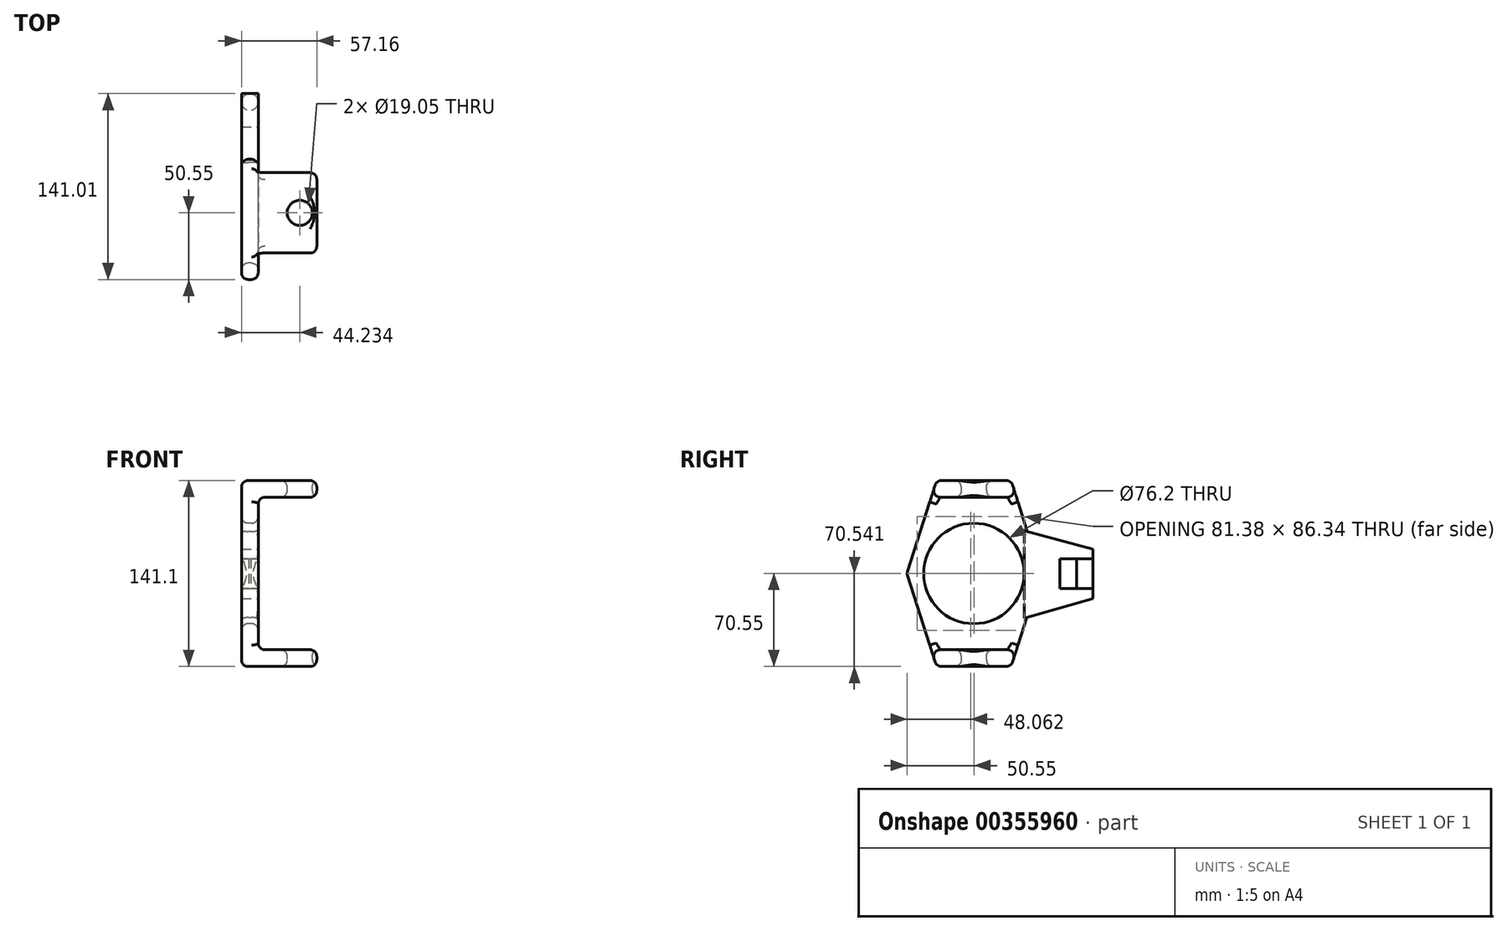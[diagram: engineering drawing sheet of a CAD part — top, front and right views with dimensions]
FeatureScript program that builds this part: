
annotation { "Feature Type Name" : "Feature", "Feature Type Description" : "" }
export const myFeature = defineFeature(function(context is Context, id is Id, definition is map)
    precondition{}
    {
        {
            var Q0;
            Q0=qCreatedBy(makeId("Front.planeOp"),FACE);
            var sketch = newSketch(context, id + "F0", { "sketchPlane" : qUnion([Q0])});
            skLineSegment(sketch, "E0.bottom", {"start": v(22.22, 57.85) * mm, "end": v(-22.23, 57.85) * mm});
            skLineSegment(sketch, "E0.top", {"start": v(22.22, -57.85) * mm, "end": v(-22.23, -57.85) * mm});
            skLineSegment(sketch, "E0.right", {"start": v(-22.23, 57.85) * mm, "end": v(-22.23, -57.85) * mm});
            skPoint(sketch, "E0.middle", {"position": v(0, 0) * mm});
            skLineSegment(sketch, "E1.0", {"start": v(22.22, -70.55) * mm, "end": v(-34.93, -70.55) * mm});
            skLineSegment(sketch, "E1.1", {"start": v(-34.93, 70.55) * mm, "end": v(-34.93, -70.55) * mm});
            skLineSegment(sketch, "E1.2", {"start": v(22.22, 70.55) * mm, "end": v(-34.93, 70.55) * mm});
            skLineSegment(sketch, "E2", {"start": v(22.22, 70.55) * mm, "end": v(22.22, 57.85) * mm});
            skLineSegment(sketch, "E3", {"start": v(22.22, -57.85) * mm, "end": v(22.22, -70.55) * mm});
            skSolve(sketch);
        }
        {
            var Q0;
            Q0=makeQuery(id+"F0.imprint","IMPRINT",FACE,{"disambiguationData":[TD([[makeQuery(id+"F0.imprint","IMPRINT",EDGE,{"derivedFrom":sQuery(id+"F0.wireOp",EDGE,"E0.bottom")}),-1.0]])]});
            extrude(context, id + "F1", {"entities" : qUnion([Q0]), "depth" : 101.6 * mm});
        }
        {
            var Q0;
            Q0=makeQuery(id+"F1.opExtrude","SWEPT_FACE",FACE,{"disambiguationData":[OSD([sQuery(id+"F0.wireOp",EDGE,"E1.1")])]});
            var sketch = newSketch(context, id + "F2", { "sketchPlane" : qUnion([Q0])});
            skCircle(sketch, "E4", {"center": v(50.8, 0) * mm, "radius": 38.1 * mm});
            skPoint(sketch, "E4.centerSnap0", {"position": v(50.8, -70.55) * mm});
            skLineSegment(sketch, "E5.bottom", {"start": v(79.08, -70.55) * mm, "end": v(22.52, -70.55) * mm, "construction": true});
            skLineSegment(sketch, "E5.top", {"start": v(79.08, 70.55) * mm, "end": v(22.52, 70.55) * mm, "construction": true});
            skLineSegment(sketch, "E5.left", {"start": v(79.08, -70.55) * mm, "end": v(79.08, 70.55) * mm, "construction": true});
            skLineSegment(sketch, "E5.right", {"start": v(22.52, -70.55) * mm, "end": v(22.52, 70.55) * mm, "construction": true});
            skLineSegment(sketch, "E6", {"start": v(79.08, -70.55) * mm, "end": v(101.6, 0) * mm});
            skLineSegment(sketch, "E7", {"start": v(101.6, 0) * mm, "end": v(79.08, 70.55) * mm});
            skLineSegment(sketch, "E8", {"start": v(22.52, 70.55) * mm, "end": v(0, 0) * mm});
            skLineSegment(sketch, "E9", {"start": v(0, 0) * mm, "end": v(22.52, -70.55) * mm});
            skSolve(sketch);
        }
        {
            var Q0;
            {var subQ0=sQuery(id+"F2.wireOp",EDGE,"E9");Q0=makeQuery(id+"F2.imprint","IMPRINT",FACE,{"disambiguationData":[TD([[makeQuery(id+"F2.imprint","IMPRINT",EDGE,{"derivedFrom":subQ0}),-1.0]])]});}
            var Q1;
            {var subQ0=sQuery(id+"F2.wireOp",EDGE,"E8");Q1=makeQuery(id+"F2.imprint","IMPRINT",FACE,{"disambiguationData":[TD([[makeQuery(id+"F2.imprint","IMPRINT",EDGE,{"derivedFrom":subQ0}),-1.0]])]});}
            var Q2;
            {var subQ0=sQuery(id+"F2.wireOp",EDGE,"E7");Q2=makeQuery(id+"F2.imprint","IMPRINT",FACE,{"disambiguationData":[TD([[makeQuery(id+"F2.imprint","IMPRINT",EDGE,{"derivedFrom":subQ0}),-1.0]])]});}
            var Q3;
            {var subQ0=sQuery(id+"F2.wireOp",EDGE,"E6");Q3=makeQuery(id+"F2.imprint","IMPRINT",FACE,{"disambiguationData":[TD([[makeQuery(id+"F2.imprint","IMPRINT",EDGE,{"derivedFrom":subQ0}),-1.0]])]});}
            var Q4;
            Q4=makeQuery(id+"F2.imprint","IMPRINT",FACE,{"disambiguationData":[TD([[makeQuery(id+"F2.imprint","IMPRINT",EDGE,{"derivedFrom":sQuery(id+"F2.wireOp",EDGE,"E4")}),1.0]])]});
            extrude(context, id + "F3", {"entities" : qUnion([Q0, Q1, Q2, Q3, Q4]), "operationType" : NewBodyOperationType.REMOVE, "endBound" : BoundingType.THROUGH_ALL, "oppositeDirection" : true, "depth" : 25.4 * mm});
        }
        {
            var Q0;
            Q0=makeQuery(id+"F1.opExtrude","SWEPT_FACE",FACE,{"disambiguationData":[OSD([sQuery(id+"F0.wireOp",EDGE,"E1.2")])]});
            var sketch = newSketch(context, id + "F4", { "sketchPlane" : qUnion([Q0])});
            skCircle(sketch, "E10", {"center": v(9.3, -50.8) * mm, "radius": 9.53 * mm});
            skPoint(sketch, "E10.centerSnap0", {"position": v(22.22, -50.8) * mm});
            skSolve(sketch);
        }
        {
            var Q0;
            Q0=makeQuery(id+"F4.imprint","IMPRINT",FACE,{"disambiguationData":[TD([[makeQuery(id+"F4.imprint","IMPRINT",EDGE,{"derivedFrom":sQuery(id+"F4.wireOp",EDGE,"E10")}),1.0]])]});
            extrude(context, id + "F5", {"entities" : qUnion([Q0]), "operationType" : NewBodyOperationType.REMOVE, "endBound" : BoundingType.THROUGH_ALL, "oppositeDirection" : true, "depth" : 25.4 * mm});
        }
        {
            var Q0;
            Q0=makeQuery(id+"F3.boolean.opBoolean","COPY",EDGE,{"derivedFrom":makeQuery(id+"F3.opExtrude","SWEPT_EDGE",EDGE,{"disambiguationData":[OSD([sQuery(id+"F0.wireOp",EDGE,"E1.1"),sQuery(id+"F0.wireOp",EDGE,"E1.2"),sQuery(id+"F2.wireOp",EDGE,"E8")])]})});
            var Q1;
            Q1=makeQuery(id+"F1.opExtrude","SWEPT_EDGE",EDGE,{"disambiguationData":[OSD([sQuery(id+"F0.wireOp",EDGE,"E1.1"),sQuery(id+"F0.wireOp",EDGE,"E1.2")])]});
            var Q2;
            Q2=makeQuery(id+"F3.boolean.opBoolean","COPY",EDGE,{"derivedFrom":makeQuery(id+"F3.opExtrude","SWEPT_EDGE",EDGE,{"disambiguationData":[OSD([sQuery(id+"F0.wireOp",EDGE,"E1.1"),sQuery(id+"F0.wireOp",EDGE,"E1.2"),sQuery(id+"F2.wireOp",EDGE,"E7")])]})});
            var Q3;
            Q3=makeQuery(id+"F1.opExtrude","SWEPT_EDGE",EDGE,{"disambiguationData":[OSD([sQuery(id+"F0.wireOp",EDGE,"E1.2"),sQuery(id+"F0.wireOp",EDGE,"E2")])]});
            var Q4;
            Q4=makeQuery(id+"F1.opExtrude","SWEPT_FACE",FACE,{"disambiguationData":[OSD([sQuery(id+"F0.wireOp",EDGE,"E1.1")])]});
            var Q5;
            Q5=makeQuery(id+"F3.boolean.opBoolean","COPY",FACE,{"derivedFrom":makeQuery(id+"F3.opExtrude","SWEPT_FACE",FACE,{"disambiguationData":[OSD([sQuery(id+"F2.wireOp",EDGE,"E8")])]})});
            var Q6;
            Q6=makeQuery(id+"F3.boolean.opBoolean","COPY",FACE,{"derivedFrom":makeQuery(id+"F3.opExtrude","SWEPT_FACE",FACE,{"disambiguationData":[OSD([sQuery(id+"F2.wireOp",EDGE,"E9")])]})});
            var Q7;
            Q7=makeQuery(id+"F1.opExtrude","SWEPT_FACE",FACE,{"disambiguationData":[OSD([sQuery(id+"F0.wireOp",EDGE,"E1.0")])]});
            var Q8;
            Q8=makeQuery(id+"F3.boolean.opBoolean","COPY",FACE,{"derivedFrom":makeQuery(id+"F3.opExtrude","SWEPT_FACE",FACE,{"disambiguationData":[OSD([sQuery(id+"F2.wireOp",EDGE,"E6")])]})});
            var Q9;
            Q9=makeQuery(id+"F3.boolean.opBoolean","COPY",FACE,{"derivedFrom":makeQuery(id+"F3.opExtrude","SWEPT_FACE",FACE,{"disambiguationData":[OSD([sQuery(id+"F2.wireOp",EDGE,"E7")])]})});
            var Q10;
            Q10=makeQuery(id+"F1.opExtrude","SWEPT_FACE",FACE,{"disambiguationData":[OSD([sQuery(id+"F0.wireOp",EDGE,"E0.bottom")])]});
            var Q11;
            Q11=makeQuery(id+"F1.opExtrude","SWEPT_FACE",FACE,{"disambiguationData":[OSD([sQuery(id+"F0.wireOp",EDGE,"E0.top")])]});
            var Q12;
            Q12=makeQuery(id+"F1.opExtrude","SWEPT_FACE",FACE,{"disambiguationData":[OSD([sQuery(id+"F0.wireOp",EDGE,"E1.2")])]});
            var Q13;
            Q13=makeQuery(id+"F3.boolean.opBoolean","INTERSECT",EDGE,{"derivedFrom":[makeQuery(id+"F1.opExtrude","SWEPT_FACE",FACE,{"disambiguationData":[OSD([sQuery(id+"F0.wireOp",EDGE,"E0.right")])]}),makeQuery(id+"F3.opExtrude","SWEPT_FACE",FACE,{"disambiguationData":[OSD([sQuery(id+"F2.wireOp",EDGE,"E4")])]})]});
            fillet(context, id + "F6", {"entities" : qUnion([Q0, Q1, Q2, Q3, Q4, Q5, Q6, Q7, Q8, Q9, Q10, Q11, Q12, Q13]), "radius" : 5.08 * mm, "tangentPropagation" : true, "allowEdgeOverflow" : false});
        }
        {
            var Q0;
            Q0=qCreatedBy(makeId("Right.planeOp"),FACE);
            var sketch = newSketch(context, id + "F7", { "sketchPlane" : qUnion([Q0])});
            skLineSegment(sketch, "E11.left", {"start": v(-12.6, 32.52) * mm, "end": v(-12.6, -33.96) * mm});
            skLineSegment(sketch, "E12.right", {"start": v(-12.6, -11.3) * mm, "end": v(-12.6, 11.3) * mm, "construction": true});
            skPoint(sketch, "E12.middle", {"position": v(27.22, 0) * mm});
            skPoint(sketch, "E12.middle.positionSnap0", {"position": v(27.22, 32.52) * mm});
            skPoint(sketch, "E12.centerSnap0", {"position": v(27.22, 32.52) * mm});
            skLineSegment(sketch, "E13", {"start": v(-12.6, 32.52) * mm, "end": v(39.66, 18.6) * mm});
            skLineSegment(sketch, "E14", {"start": v(39.66, -19.09) * mm, "end": v(-12.6, -33.96) * mm});
            skLineSegment(sketch, "E15", {"start": v(39.66, 18.6) * mm, "end": v(39.66, 11.3) * mm});
            skLineSegment(sketch, "E16.trimOffspring", {"start": v(39.66, -11.3) * mm, "end": v(39.66, -19.09) * mm});
            skLineSegment(sketch, "E17", {"start": v(39.66, -19.09) * mm, "end": v(39.66, -11.3) * mm});
            skLineSegment(sketch, "E18.bottom", {"start": v(39.66, -11.3) * mm, "end": v(14.3, -11.3) * mm});
            skLineSegment(sketch, "E18.top", {"start": v(39.66, 11.3) * mm, "end": v(14.3, 11.3) * mm});
            skLineSegment(sketch, "E18.right", {"start": v(14.3, -11.3) * mm, "end": v(14.3, 11.3) * mm});
            skPoint(sketch, "E19.orphan", {"position": v(39.66, -33.96) * mm});
            skPoint(sketch, "E20.start.orphan", {"position": v(67.05, -11.3) * mm});
            skPoint(sketch, "E11.right.end.orphan", {"position": v(67.05, 11.3) * mm});
            skPoint(sketch, "E11.bottom.end.orphan", {"position": v(67.05, 32.52) * mm});
            skLineSegment(sketch, "E21.trimOffspring", {"start": v(39.66, 11.3) * mm, "end": v(39.66, 18.6) * mm});
            skSolve(sketch);
        }
        {
            var Q0;
            Q0=makeQuery(id+"F7.imprint","IMPRINT",FACE,{"disambiguationData":[TD([[makeQuery(id+"F7.imprint","IMPRINT",EDGE,{"derivedFrom":sQuery(id+"F7.wireOp",EDGE,"E11.left")}),1.0]])]});
            var Q1;
            Q1=makeQuery(id+"F1.opExtrude","SWEPT_FACE",FACE,{"disambiguationData":[OSD([sQuery(id+"F0.wireOp",EDGE,"E0.right")])]});
            extrude(context, id + "F8", {"entities" : qUnion([Q0]), "operationType" : NewBodyOperationType.ADD, "oppositeDirection" : true, "depth" : 34.92 * mm, "hasSecondDirection" : true, "secondDirectionBound" : SecondDirectionBoundingType.UP_TO_SURFACE, "secondDirectionOppositeDirection" : true, "secondDirectionBoundEntityFace" : qUnion([Q1]), "secondDirectionDepth" : 25.4 * mm});
        }
        {
            var Q0;
            Q0=makeQuery(id+"F8.opExtrude","SWEPT_FACE",FACE,{"disambiguationData":[OSD([sQuery(id+"F7.wireOp",EDGE,"E18.bottom")])]});
            var sketch = newSketch(context, id + "F9", { "sketchPlane" : qUnion([Q0])});
            skCircle(sketch, "E22", {"center": v(-28.58, 33.36) * mm, "radius": 6.35 * mm});
            skPoint(sketch, "E22.centerSnap0", {"position": v(-28.58, 39.66) * mm});
            skSolve(sketch);
        }
        {
            var Q0;
            {var subQ0=sQuery(id+"F9.wireOp",EDGE,"E22");var subQ1=sQuery(id+"F7.wireOp",EDGE,"E18.bottom");var subQ6=makeQuery(id+"F9.imprint","INTERSECT",VERTEX,{"derivedFrom":[makeQuery(id+"F8.opExtrude","CAP_EDGE",EDGE,{"disambiguationData":[OSD([subQ1])],"isStart":false}),subQ0]});Q0=makeQuery(id+"F9.imprint","IMPRINT",FACE,{"disambiguationData":[TD([[makeQuery(id+"F9.imprint","IMPRINT",EDGE,{"disambiguationData":[TD([[subQ6,1.0]])],"derivedFrom":subQ0}),1.0]])]});}
            var Q1;
            Q1=makeQuery(id+"F8.opExtrude","SWEPT_FACE",FACE,{"disambiguationData":[OSD([sQuery(id+"F7.wireOp",EDGE,"E18.top")])]});
            extrude(context, id + "F10", {"entities" : qUnion([Q0]), "operationType" : NewBodyOperationType.ADD, "endBound" : BoundingType.UP_TO_SURFACE, "endBoundEntityFace" : qUnion([Q1]), "depth" : 25.4 * mm});
        }
    });
